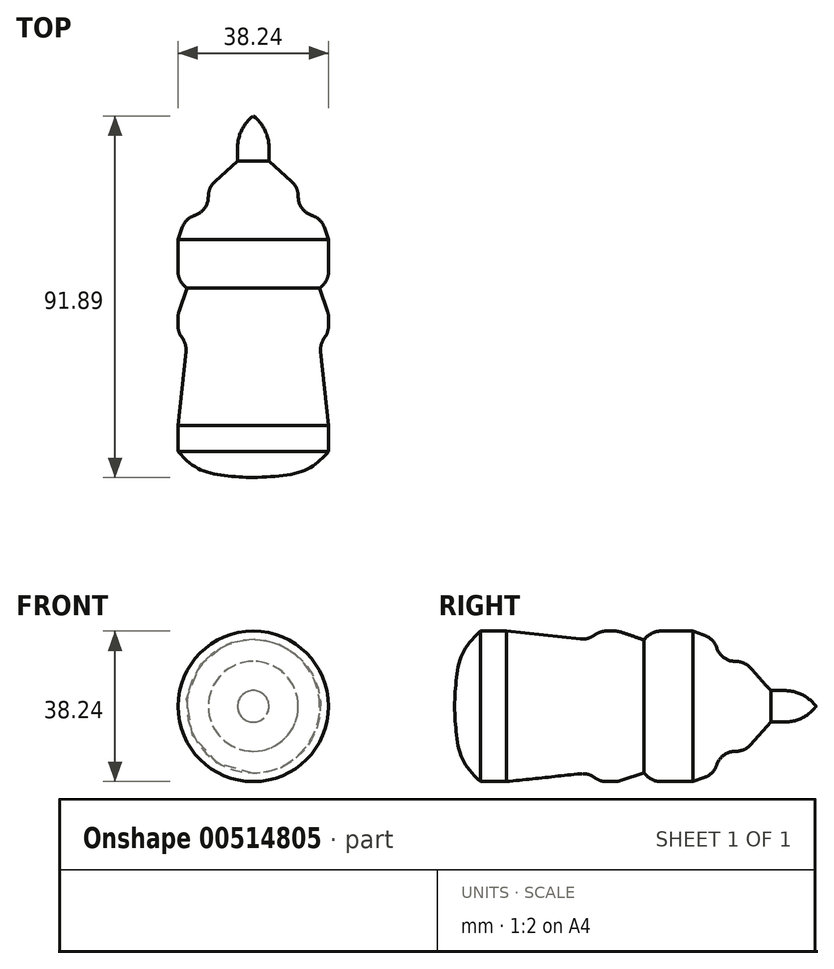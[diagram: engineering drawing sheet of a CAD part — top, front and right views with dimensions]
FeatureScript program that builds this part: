
annotation { "Feature Type Name" : "Feature", "Feature Type Description" : "" }
export const myFeature = defineFeature(function(context is Context, id is Id, definition is map)
    precondition{}
    {
        {
            var Q0;
            Q0=qCreatedBy(makeId("Top.planeOp"),FACE);
            var sketch = newSketch(context, id + "F0", { "sketchPlane" : qUnion([Q0])});
            skLineSegment(sketch, "E0", {"start": v(0, 45.27) * mm, "end": v(4, 41.8) * mm});
            skLineSegment(sketch, "E1", {"start": v(4, 41.8) * mm, "end": v(4, 33.74) * mm});
            skLineSegment(sketch, "E2", {"start": v(4, 33.74) * mm, "end": v(11.42, 27.11) * mm});
            skLineSegment(sketch, "E3", {"start": v(11.42, 27.11) * mm, "end": v(11.42, 22.21) * mm});
            skLineSegment(sketch, "E4", {"start": v(11.42, 22.21) * mm, "end": v(11.42, 20.25) * mm});
            skLineSegment(sketch, "E5", {"start": v(11.42, 20.25) * mm, "end": v(16.88, 20.25) * mm});
            skLineSegment(sketch, "E6", {"start": v(16.88, 20.25) * mm, "end": v(19.12, 13.9) * mm});
            skLineSegment(sketch, "E7", {"start": v(19.12, 13.9) * mm, "end": v(19.12, 10.91) * mm});
            skLineSegment(sketch, "E8", {"start": v(19.12, 10.91) * mm, "end": v(19.12, 3.44) * mm});
            skLineSegment(sketch, "E9", {"start": v(19.12, 3.44) * mm, "end": v(16.88, 1.57) * mm});
            skLineSegment(sketch, "E10", {"start": v(16.88, 1.57) * mm, "end": v(19.12, -5.16) * mm});
            skLineSegment(sketch, "E11", {"start": v(19.12, -5.16) * mm, "end": v(19.12, -10.39) * mm});
            skLineSegment(sketch, "E12", {"start": v(19.12, -10.39) * mm, "end": v(16.88, -12.26) * mm});
            skLineSegment(sketch, "E13", {"start": v(16.88, -12.26) * mm, "end": v(19.12, -33.41) * mm});
            skLineSegment(sketch, "E14", {"start": v(19.12, -33.41) * mm, "end": v(19.12, -40.04) * mm});
            skFitSpline(sketch, "E15", {"points": [v(19.12, -40.04) * mm, v(13.1, -44.74) * mm, v(0, -46.62) * mm], "startDerivative": vector(-11.96, -12.55) * mm, "endDerivative": vector(-25.65, -1.13) * mm});
            skLineSegment(sketch, "E16", {"start": v(0, 45.27) * mm, "end": v(0, -46.62) * mm});
            skSolve(sketch);
        }
        {
            var Q0;
            Q0 = qSketchRegion(id + "F0", true);
            var Q1;
            Q1=sQuery(id+"F0.wireOp",EDGE,"E16");
            revolve(context, id + "F1", {"entities" : qUnion([Q0]), "axis" : qUnion([Q1]), "revolveType" : RevolveType.FULL});
        }
        {
            var Q0;
            Q0=makeQuery(id+"F1.opRevolve","SWEPT_FACE",FACE,{"disambiguationData":[OSD([sQuery(id+"F0.wireOp",EDGE,"E0")])]});
            fillet(context, id + "F2", {"entities" : qUnion([Q0]), "radius" : 10.04 * mm, "tangentPropagation" : true, "allowEdgeOverflow" : false});
        }
        {
            var Q0;
            Q0=makeQuery(id+"F1.opRevolve","SWEPT_EDGE",EDGE,{"disambiguationData":[OSD([sQuery(id+"F0.wireOp",EDGE,"E5"),sQuery(id+"F0.wireOp",EDGE,"E6")])]});
            fillet(context, id + "F3", {"entities" : qUnion([Q0]), "radius" : 5 * mm, "tangentPropagation" : true, "allowEdgeOverflow" : false});
        }
        {
            var Q0;
            Q0=makeQuery(id+"F1.opRevolve","SWEPT_EDGE",EDGE,{"disambiguationData":[OSD([sQuery(id+"F0.wireOp",EDGE,"E10"),sQuery(id+"F0.wireOp",EDGE,"E11")])]});
            fillet(context, id + "F4", {"entities" : qUnion([Q0]), "radius" : 5 * mm, "tangentPropagation" : true, "allowEdgeOverflow" : false});
        }
        {
            var Q0;
            Q0=makeQuery(id+"F1.opRevolve","SWEPT_EDGE",EDGE,{"disambiguationData":[OSD([sQuery(id+"F0.wireOp",EDGE,"E2"),sQuery(id+"F0.wireOp",EDGE,"E3")])]});
            fillet(context, id + "F5", {"entities" : qUnion([Q0]), "radius" : 5 * mm, "tangentPropagation" : true, "allowEdgeOverflow" : false});
        }
        {
            var Q0;
            Q0=makeQuery(id+"F1.opRevolve","SWEPT_EDGE",EDGE,{"disambiguationData":[OSD([sQuery(id+"F0.wireOp",EDGE,"E4"),sQuery(id+"F0.wireOp",EDGE,"E5")])]});
            fillet(context, id + "F6", {"entities" : qUnion([Q0]), "radius" : 5 * mm, "tangentPropagation" : true, "allowEdgeOverflow" : false});
        }
        {
            var Q0;
            Q0=makeQuery(id+"F1.opRevolve","SWEPT_EDGE",EDGE,{"disambiguationData":[OSD([sQuery(id+"F0.wireOp",EDGE,"E11"),sQuery(id+"F0.wireOp",EDGE,"E12")])]});
            fillet(context, id + "F7", {"entities" : qUnion([Q0]), "radius" : 5 * mm, "tangentPropagation" : true, "allowEdgeOverflow" : false});
        }
        {
            var Q0;
            Q0=makeQuery(id+"F1.opRevolve","SWEPT_EDGE",EDGE,{"disambiguationData":[OSD([sQuery(id+"F0.wireOp",EDGE,"E12"),sQuery(id+"F0.wireOp",EDGE,"E13")])]});
            fillet(context, id + "F8", {"entities" : qUnion([Q0]), "radius" : 5 * mm, "tangentPropagation" : true, "allowEdgeOverflow" : false});
        }
        {
            var Q0;
            Q0=makeQuery(id+"F1.opRevolve","SWEPT_EDGE",EDGE,{"disambiguationData":[OSD([sQuery(id+"F0.wireOp",EDGE,"E8"),sQuery(id+"F0.wireOp",EDGE,"E9")])]});
            fillet(context, id + "F9", {"entities" : qUnion([Q0]), "radius" : 5 * mm, "tangentPropagation" : true, "allowEdgeOverflow" : false});
        }
    });
